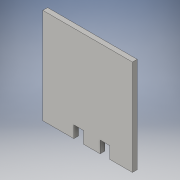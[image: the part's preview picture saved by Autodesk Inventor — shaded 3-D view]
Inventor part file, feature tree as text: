
AUTODESK INVENTOR PART (.ipt)
format: ipt  version: 2016 (Build 200138000, 138)  size: 106,496 bytes
history: native  units: in
note: dims shown in document units (in); Inventor stores cm internally (conversion verified against a paired STEP export)
features: sketch x2, extrude x1
ambient origin geometry x8: Origin, YZ Plane, XZ Plane, XY Plane, X Axis, Y Axis, Z Axis, Center Point
bodies: Solid1 (feature_tree)
feature tree (3):
  sketch  "Sketch1"  dims[d1=10.0in d2=5.125in]
  extrude  "Extrusion1"  Depth=5.125in
  sketch  "Sketch2"  dims[d3=0.875in d4=1.0in d5=0.875in d6=1.0in d7=1.25in d8=0.5in d9=0.0in]
